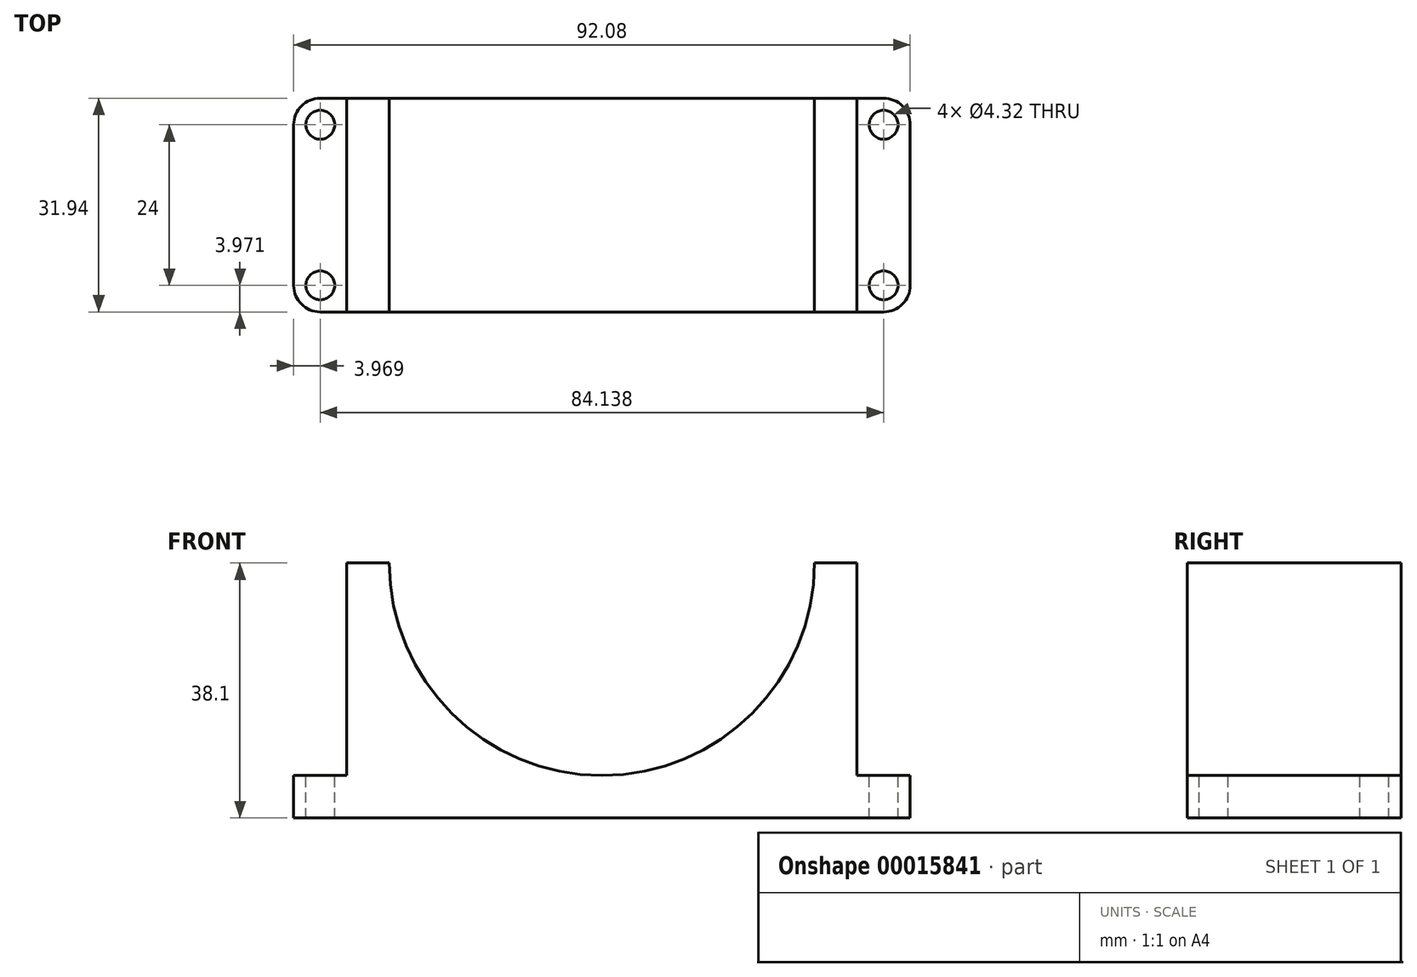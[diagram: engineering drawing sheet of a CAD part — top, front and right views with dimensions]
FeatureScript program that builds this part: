
annotation { "Feature Type Name" : "Feature", "Feature Type Description" : "" }
export const myFeature = defineFeature(function(context is Context, id is Id, definition is map)
    precondition{}
    {
        {
            var Q0;
            Q0=qCreatedBy(makeId("Top.planeOp"),FACE);
            var sketch = newSketch(context, id + "F0", { "sketchPlane" : qUnion([Q0])});
            skLineSegment(sketch, "E0.bottom", {"start": v(0, 0) * mm, "end": v(92.08, 0) * mm});
            skLineSegment(sketch, "E0.top", {"start": v(0, -31.94) * mm, "end": v(92.08, -31.94) * mm});
            skLineSegment(sketch, "E0.left", {"start": v(0, 0) * mm, "end": v(0, -31.94) * mm});
            skLineSegment(sketch, "E0.right", {"start": v(92.08, 0) * mm, "end": v(92.08, -31.94) * mm});
            skSolve(sketch);
        }
        {
            var Q0;
            Q0 = qSketchRegion(id + "F0", true);
            extrude(context, id + "F1", {"entities" : qUnion([Q0]), "depth" : 38.1 * mm});
        }
        {
            var Q0;
            Q0=makeQuery(id+"F1.opExtrude","SWEPT_FACE",FACE,{"disambiguationData":[OSD([sQuery(id+"F0.wireOp",EDGE,"E0.top")])]});
            var sketch = newSketch(context, id + "F2", { "sketchPlane" : qUnion([Q0])});
            skArc(sketch, "E1", {"start": v(14.29, 38.1) * mm, "mid": v(46.04, 6.35) * mm, "end": v(77.79, 38.1) * mm});
            skLineSegment(sketch, "E2", {"start": v(14.29, 38.1) * mm, "end": v(77.79, 38.1) * mm});
            skSolve(sketch);
        }
        {
            var Q0;
            Q0 = qSketchRegion(id + "F2", true);
            var Q1;
            Q1=makeQuery(id+"F1.opExtrude","SWEPT_FACE",FACE,{"disambiguationData":[OSD([sQuery(id+"F0.wireOp",EDGE,"E0.bottom")])]});
            extrude(context, id + "F3", {"entities" : qUnion([Q0]), "operationType" : NewBodyOperationType.REMOVE, "endBound" : BoundingType.UP_TO_SURFACE, "oppositeDirection" : true, "endBoundEntityFace" : qUnion([Q1]), "depth" : 25.4 * mm});
        }
        {
            var Q0;
            {var subQ0=sQuery(id+"F0.wireOp",EDGE,"E0.bottom");var subQ1=sQuery(id+"F0.wireOp",EDGE,"E0.top");var subQ2=sQuery(id+"F0.wireOp",EDGE,"E0.right");Q0=makeQuery(id+"F3.boolean.opBoolean","SPLIT",FACE,{"disambiguationData":[TD([makeQuery(id+"F1.opExtrude","SWEPT_FACE",FACE,{"disambiguationData":[OSD([subQ2])]})])],"derivedFrom":makeQuery(id+"F1.opExtrude","CAP_FACE",FACE,{"disambiguationData":[OSD([subQ0,subQ1,sQuery(id+"F0.wireOp",EDGE,"E0.left"),subQ2])],"isStart":false})});}
            var sketch = newSketch(context, id + "F4", { "sketchPlane" : qUnion([Q0])});
            skLineSegment(sketch, "E3.bottom", {"start": v(92.08, 0) * mm, "end": v(84.14, 0) * mm});
            skLineSegment(sketch, "E3.top", {"start": v(92.08, -31.94) * mm, "end": v(84.14, -31.94) * mm});
            skLineSegment(sketch, "E3.left", {"start": v(92.08, 0) * mm, "end": v(92.08, -31.94) * mm});
            skLineSegment(sketch, "E3.right", {"start": v(84.14, 0) * mm, "end": v(84.14, -31.94) * mm});
            skLineSegment(sketch, "E4.bottom", {"start": v(0, 0) * mm, "end": v(7.94, 0) * mm});
            skLineSegment(sketch, "E4.top", {"start": v(0, -31.94) * mm, "end": v(7.94, -31.94) * mm});
            skLineSegment(sketch, "E4.left", {"start": v(0, 0) * mm, "end": v(0, -31.94) * mm});
            skLineSegment(sketch, "E4.right", {"start": v(7.94, 0) * mm, "end": v(7.94, -31.94) * mm});
            skSolve(sketch);
        }
        {
            var Q0;
            Q0 = qSketchRegion(id + "F4", true);
            extrude(context, id + "F5", {"entities" : qUnion([Q0]), "operationType" : NewBodyOperationType.REMOVE, "oppositeDirection" : true, "depth" : 31.75 * mm});
        }
        {
            var Q0;
            Q0=makeQuery(id+"F5.boolean.opBoolean","COPY",FACE,{"derivedFrom":makeQuery(id+"F5.opExtrude","CAP_FACE",FACE,{"disambiguationData":[OSD([sQuery(id+"F4.wireOp",EDGE,"E4.bottom"),sQuery(id+"F4.wireOp",EDGE,"E4.top"),sQuery(id+"F4.wireOp",EDGE,"E4.left"),sQuery(id+"F4.wireOp",EDGE,"E4.right")])],"isStart":false})});
            var sketch = newSketch(context, id + "F6", { "sketchPlane" : qUnion([Q0])});
            skLineSegment(sketch, "E5", {"start": v(3.97, 0) * mm, "end": v(3.97, -3.97) * mm});
            skLineSegment(sketch, "E6", {"start": v(3.97, -31.94) * mm, "end": v(3.97, -27.97) * mm});
            skLineSegment(sketch, "E7", {"start": v(3.97, -27.97) * mm, "end": v(0, -27.97) * mm});
            skLineSegment(sketch, "E8", {"start": v(88.1, -31.94) * mm, "end": v(88.1, -27.97) * mm});
            skLineSegment(sketch, "E9", {"start": v(88.1, 0) * mm, "end": v(88.1, -3.97) * mm});
            skCircle(sketch, "E10", {"center": v(3.97, -27.97) * mm, "radius": 2.16 * mm});
            skCircle(sketch, "E11", {"center": v(3.97, -3.97) * mm, "radius": 2.16 * mm});
            skCircle(sketch, "E12", {"center": v(88.1, -3.97) * mm, "radius": 2.16 * mm});
            skCircle(sketch, "E13", {"center": v(88.1, -27.97) * mm, "radius": 2.16 * mm});
            skSolve(sketch);
        }
        {
            var Q0;
            Q0 = qSketchRegion(id + "F6", true);
            var Q1;
            Q1=makeQuery(id+"F1.opExtrude","CAP_FACE",FACE,{"disambiguationData":[OSD([sQuery(id+"F0.wireOp",EDGE,"E0.bottom"),sQuery(id+"F0.wireOp",EDGE,"E0.top"),sQuery(id+"F0.wireOp",EDGE,"E0.left"),sQuery(id+"F0.wireOp",EDGE,"E0.right")])],"isStart":true});
            extrude(context, id + "F7", {"entities" : qUnion([Q0]), "operationType" : NewBodyOperationType.REMOVE, "endBound" : BoundingType.UP_TO_SURFACE, "oppositeDirection" : true, "endBoundEntityFace" : qUnion([Q1]), "depth" : 25.4 * mm});
        }
        {
            var Q0;
            Q0=makeQuery(id+"F1.opExtrude","SWEPT_EDGE",EDGE,{"disambiguationData":[OSD([sQuery(id+"F0.wireOp",EDGE,"E0.bottom"),sQuery(id+"F0.wireOp",EDGE,"E0.left")])]});
            var Q1;
            Q1=makeQuery(id+"F1.opExtrude","SWEPT_EDGE",EDGE,{"disambiguationData":[OSD([sQuery(id+"F0.wireOp",EDGE,"E0.top"),sQuery(id+"F0.wireOp",EDGE,"E0.left")])]});
            var Q2;
            Q2=makeQuery(id+"F1.opExtrude","SWEPT_EDGE",EDGE,{"disambiguationData":[OSD([sQuery(id+"F0.wireOp",EDGE,"E0.top"),sQuery(id+"F0.wireOp",EDGE,"E0.right")])]});
            var Q3;
            Q3=makeQuery(id+"F1.opExtrude","SWEPT_EDGE",EDGE,{"disambiguationData":[OSD([sQuery(id+"F0.wireOp",EDGE,"E0.bottom"),sQuery(id+"F0.wireOp",EDGE,"E0.right")])]});
            fillet(context, id + "F8", {"entities" : qUnion([Q0, Q1, Q2, Q3]), "radius" : 3.97 * mm, "tangentPropagation" : true, "allowEdgeOverflow" : false});
        }
    });
